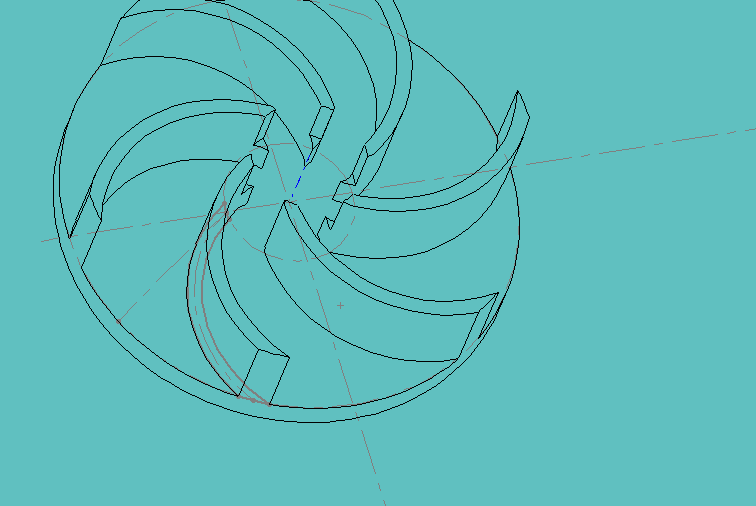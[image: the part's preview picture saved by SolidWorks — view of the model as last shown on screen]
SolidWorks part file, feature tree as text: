
SOLIDWORKS PART (.sldprt)
format: sldprt  version: not decoded by parser v0  size: 179,200 bytes
history: native  units: mm
features: sketch x4, extrude x2, material x1, pattern_circular x1, cut_extrude x1 (+12 scaffold rows collapsed)
feature tree (21):
  scaffold x12  (default folders/planes/origin — collapsed)
  material  "Material <not specified>"
  sketch  "Sketch1"  dims[D1=63.0mm]
  extrude  "Extrude1"  Depth=4mm
  sketch  "Sketch2"  dims[c1.D1=18.0mm c1.D2=70.0mm c1.D3=40.0mm c1.D4=20.0mm c2.D3=20.0mm c2.D2=19.0mm c3.D3=21.0mm c3.D4=20.0mm c3.D5=~28.160342mm c3.D6=20.0mm c3.D7=20.0mm c4.D4=12.0mm c4.D5=12.0mm c4.D6=8.0mm c5.D5=35.0mm c5.D2=2.0mm c5.D3=40.0mm c6.D5=~20.295395mm c7.D5=35.0deg c7.D2=1.0mm c7.D3=1.0mm c7.D7=1.0mm c7.D8=1.0mm]
  sketch  "Sketch8"  dims[c1.D1=11.0mm c1.D2=2.0mm c1.D3=~2.267176mm c2.D2=2.0mm c2.D3=~2.521827mm c2.D1=6.0mm c3.D2=5.0mm c3.D1=6.0mm c4.D2=1.0mm c4.D3=1.0mm]
  extrude  "Extrude2"  Depth=13mm
  pattern_circular  "CirPattern1"  Count=6 Angle=360deg
  sketch  "Sketch9"  dims[D1=16.0mm]
  cut_extrude  "Cut-Extrude1"  Depth=8mm
decode coverage: 8 of 8 modeling features carry decoded parameters
note: ~ marks probable driven/reference dimensions
note: suppression state not decoded; provenance and decode notes live in map.json
